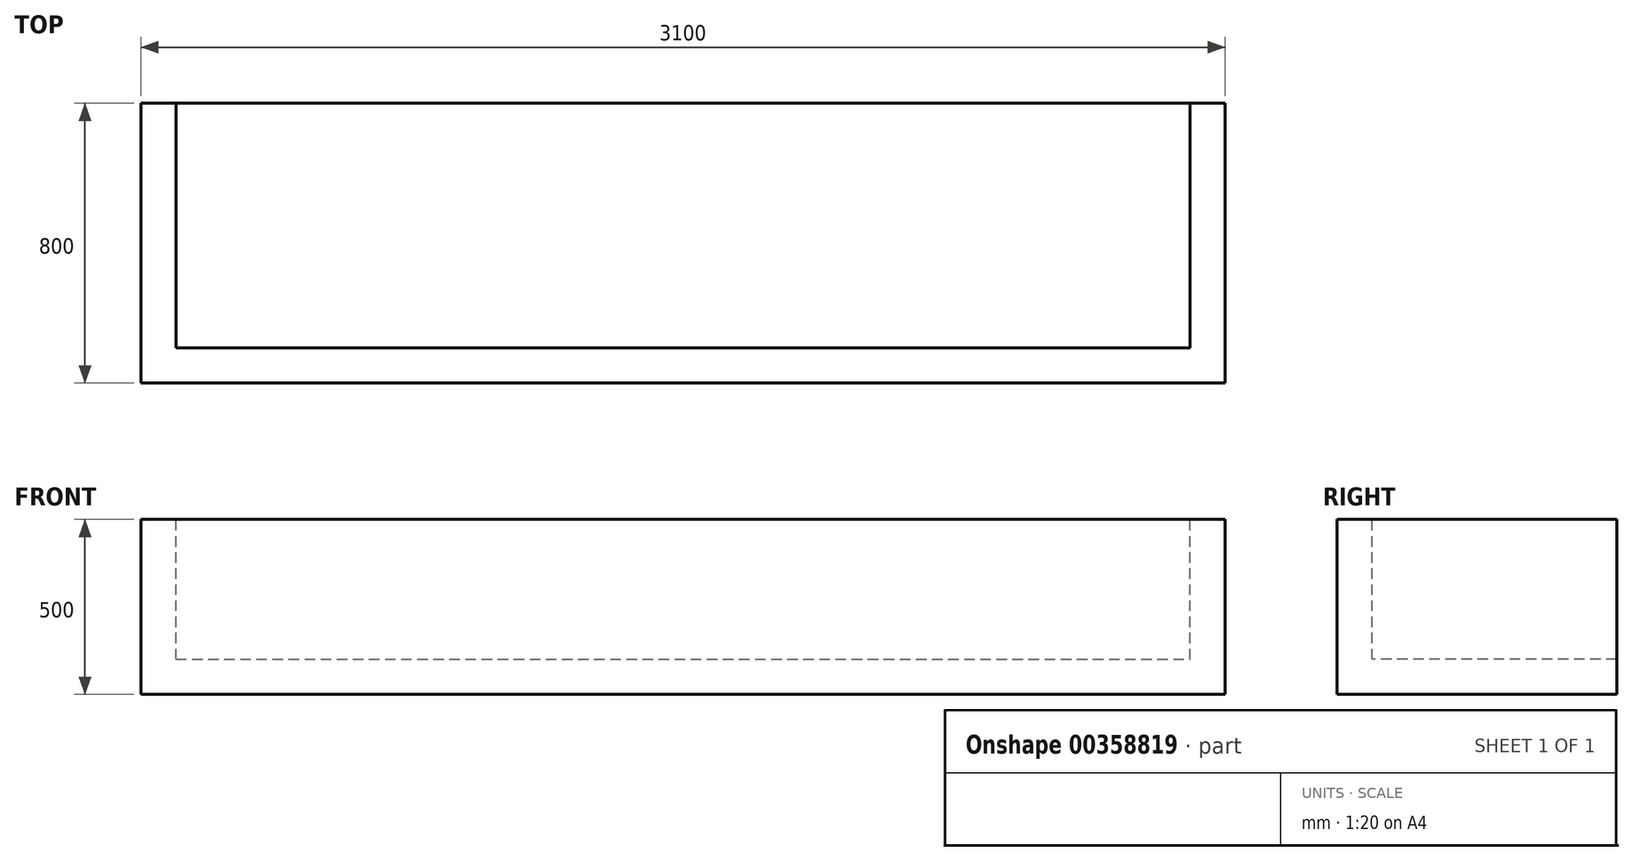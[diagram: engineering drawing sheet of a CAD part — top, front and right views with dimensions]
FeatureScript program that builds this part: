
annotation { "Feature Type Name" : "Feature", "Feature Type Description" : "" }
export const myFeature = defineFeature(function(context is Context, id is Id, definition is map)
    precondition{}
    {
        {
            var Q0;
            Q0=qCreatedBy(makeId("Top.planeOp"),FACE);
            var sketch = newSketch(context, id + "F0", { "sketchPlane" : qUnion([Q0])});
            skLineSegment(sketch, "E0", {"start": v(0, 0) * mm, "end": v(0, -800) * mm});
            skLineSegment(sketch, "E1", {"start": v(0, -800) * mm, "end": v(3100, -800) * mm});
            skLineSegment(sketch, "E2", {"start": v(3100, -800) * mm, "end": v(3100, 0) * mm});
            skLineSegment(sketch, "E3", {"start": v(3100, 0) * mm, "end": v(3000, 0) * mm});
            skLineSegment(sketch, "E4", {"start": v(3000, 0) * mm, "end": v(3000, -700) * mm});
            skLineSegment(sketch, "E5", {"start": v(3000, -700) * mm, "end": v(100, -700) * mm});
            skLineSegment(sketch, "E6", {"start": v(100, -700) * mm, "end": v(100, 0) * mm});
            skLineSegment(sketch, "E7", {"start": v(100, 0) * mm, "end": v(0, 0) * mm});
            skSolve(sketch);
        }
        {
            var Q0;
            Q0 = qSketchRegion(id + "F0", true);
            extrude(context, id + "F1", {"entities" : qUnion([Q0]), "oppositeDirection" : true, "depth" : 400 * mm});
        }
        {
            var Q0;
            Q0=makeQuery(id+"F1.opExtrude","CAP_FACE",FACE,{"disambiguationData":[OSD([sQuery(id+"F0.wireOp",EDGE,"E0"),sQuery(id+"F0.wireOp",EDGE,"E1"),sQuery(id+"F0.wireOp",EDGE,"E2"),sQuery(id+"F0.wireOp",EDGE,"E3"),sQuery(id+"F0.wireOp",EDGE,"E4"),sQuery(id+"F0.wireOp",EDGE,"E5"),sQuery(id+"F0.wireOp",EDGE,"E6"),sQuery(id+"F0.wireOp",EDGE,"E7")])],"isStart":false});
            var sketch = newSketch(context, id + "F2", { "sketchPlane" : qUnion([Q0])});
            skLineSegment(sketch, "E8.bottom", {"start": v(0, 0) * mm, "end": v(3100, 0) * mm});
            skLineSegment(sketch, "E8.top", {"start": v(0, 800) * mm, "end": v(3100, 800) * mm});
            skLineSegment(sketch, "E8.left", {"start": v(0, 0) * mm, "end": v(0, 800) * mm});
            skLineSegment(sketch, "E8.right", {"start": v(3100, 0) * mm, "end": v(3100, 800) * mm});
            skSolve(sketch);
        }
        {
            var Q0;
            Q0 = qSketchRegion(id + "F2", true);
            extrude(context, id + "F3", {"entities" : qUnion([Q0]), "operationType" : NewBodyOperationType.ADD, "depth" : 100 * mm});
        }
    });
